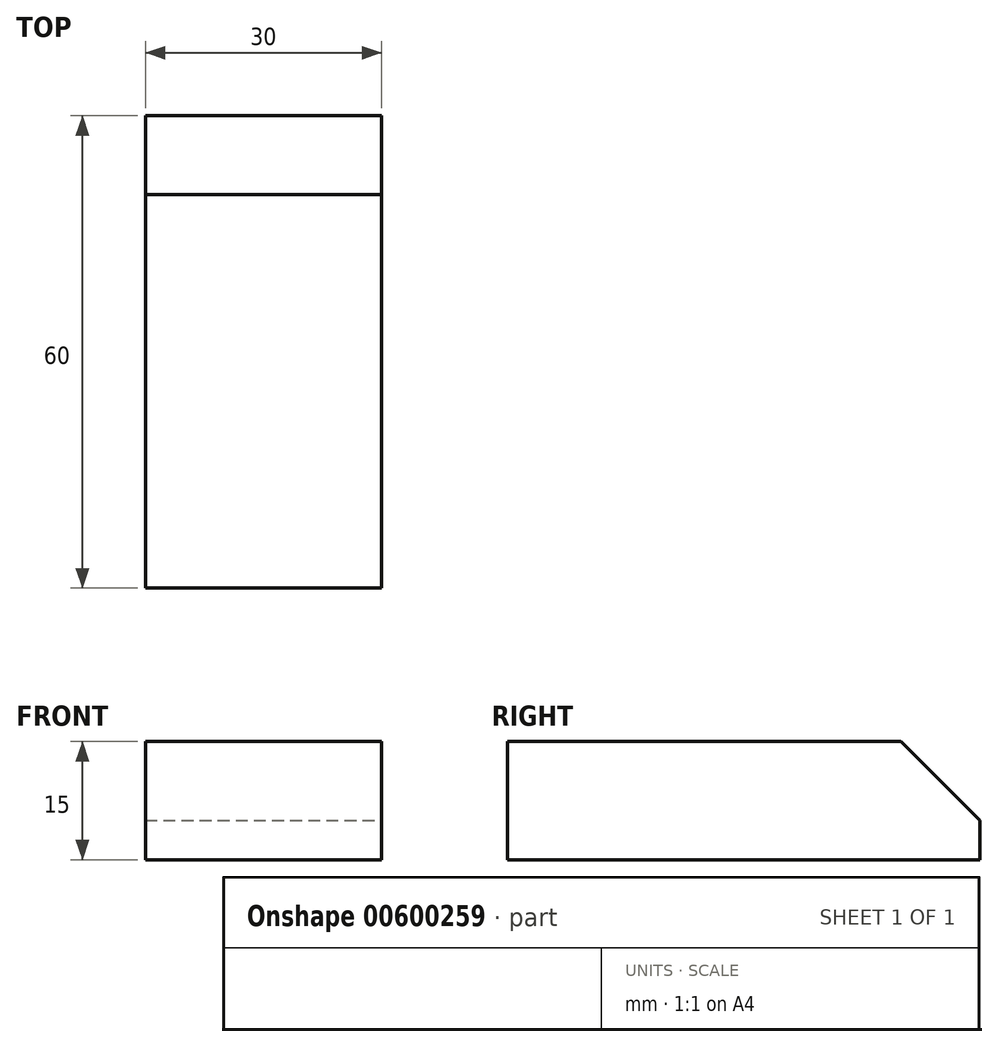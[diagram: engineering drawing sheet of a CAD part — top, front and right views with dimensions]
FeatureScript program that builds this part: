
annotation { "Feature Type Name" : "Feature", "Feature Type Description" : "" }
export const myFeature = defineFeature(function(context is Context, id is Id, definition is map)
    precondition{}
    {
        {
            var Q0;
            Q0=qCreatedBy(makeId("Right.planeOp"),FACE);
            var sketch = newSketch(context, id + "F0", { "sketchPlane" : qUnion([Q0])});
            skLineSegment(sketch, "E0.bottom", {"start": v(0, 0) * mm, "end": v(60, 0) * mm});
            skLineSegment(sketch, "E0.top", {"start": v(0, 15) * mm, "end": v(60, 15) * mm});
            skLineSegment(sketch, "E0.left", {"start": v(0, 0) * mm, "end": v(0, 15) * mm});
            skLineSegment(sketch, "E0.right", {"start": v(60, 0) * mm, "end": v(60, 15) * mm});
            skSolve(sketch);
        }
        {
            var Q0;
            Q0 = qSketchRegion(id + "F0", true);
            extrude(context, id + "F1", {"entities" : qUnion([Q0]), "depth" : 30 * mm, "offsetDistance" : 25 * mm});
        }
        {
            var Q0;
            Q0=makeQuery(id+"F1.opExtrude","CAP_FACE",FACE,{"disambiguationData":[OSD([sQuery(id+"F0.wireOp",EDGE,"E0.bottom"),sQuery(id+"F0.wireOp",EDGE,"E0.top"),sQuery(id+"F0.wireOp",EDGE,"E0.left"),sQuery(id+"F0.wireOp",EDGE,"E0.right")])],"isStart":false});
            var sketch = newSketch(context, id + "F2", { "sketchPlane" : qUnion([Q0])});
            skLineSegment(sketch, "E1", {"start": v(50, 15) * mm, "end": v(60, 5) * mm});
            skSolve(sketch);
        }
        {
            var Q0;
            {var subQ0=sQuery(id+"F2.wireOp",EDGE,"E1");Q0=makeQuery(id+"F2.imprint","IMPRINT",FACE,{"disambiguationData":[TD([[makeQuery(id+"F2.imprint","IMPRINT",EDGE,{"derivedFrom":subQ0}),1.0]])]});}
            extrude(context, id + "F3", {"entities" : qUnion([Q0]), "operationType" : NewBodyOperationType.REMOVE, "oppositeDirection" : true, "depth" : 30 * mm, "offsetDistance" : 25 * mm});
        }
    });
